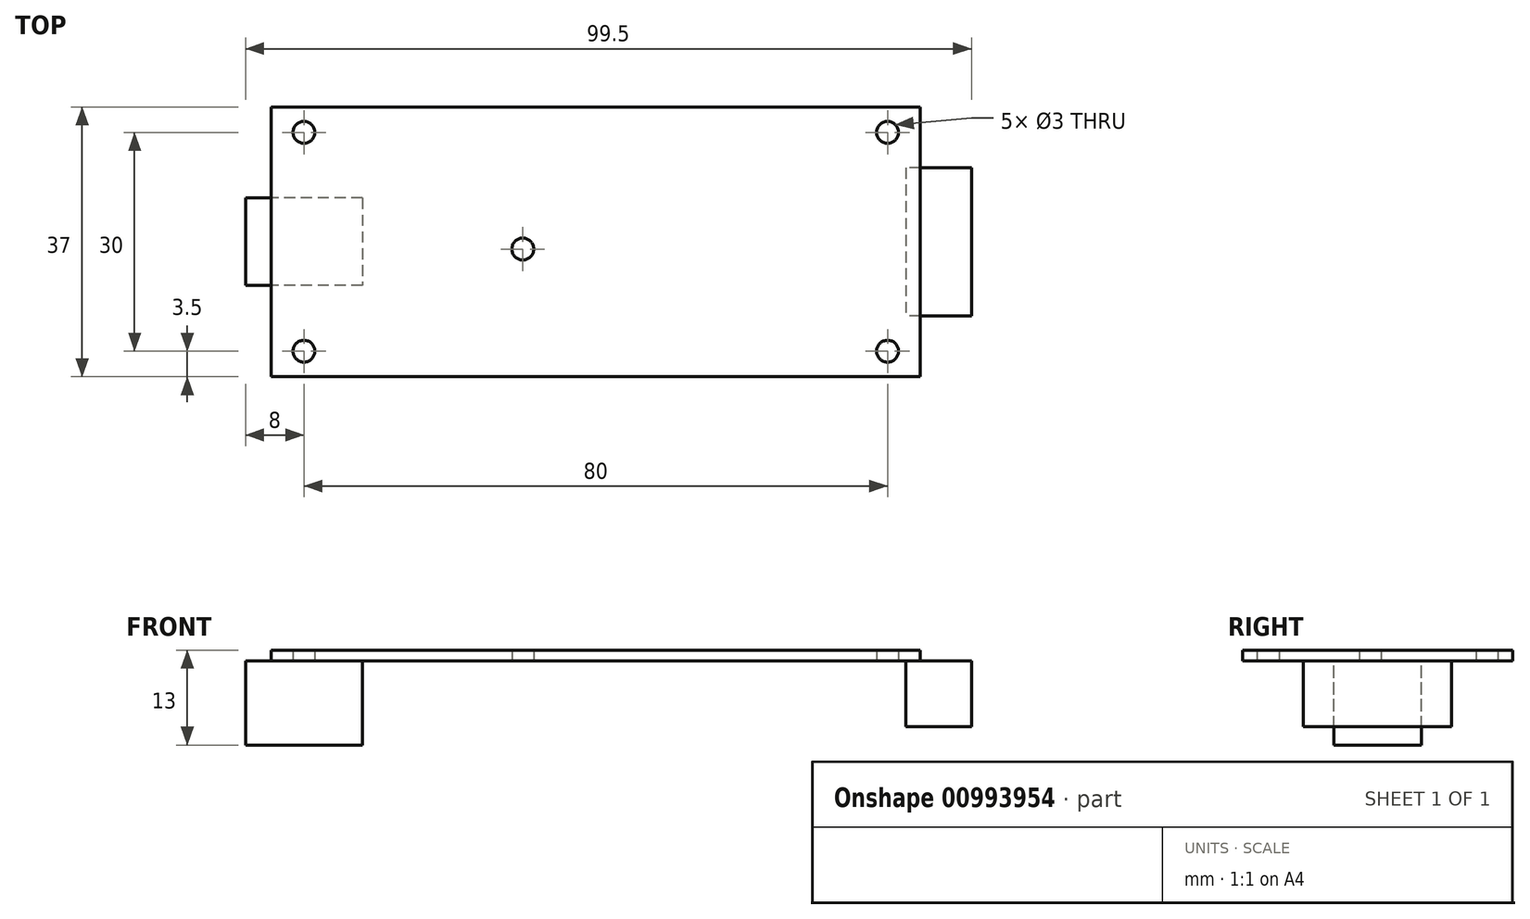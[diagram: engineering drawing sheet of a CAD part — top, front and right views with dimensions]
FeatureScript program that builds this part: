
annotation { "Feature Type Name" : "Feature", "Feature Type Description" : "" }
export const myFeature = defineFeature(function(context is Context, id is Id, definition is map)
    precondition{}
    {
        {
            var Q0;
            Q0=qCreatedBy(makeId("Top.planeOp"),FACE);
            var sketch = newSketch(context, id + "F0", { "sketchPlane" : qUnion([Q0])});
            skLineSegment(sketch, "E0.bottom", {"start": v(-44.5, 18.5) * mm, "end": v(44.5, 18.5) * mm});
            skLineSegment(sketch, "E0.top", {"start": v(-44.5, -18.5) * mm, "end": v(44.5, -18.5) * mm});
            skLineSegment(sketch, "E0.left", {"start": v(-44.5, 18.5) * mm, "end": v(-44.5, -18.5) * mm});
            skLineSegment(sketch, "E0.right", {"start": v(44.5, 18.5) * mm, "end": v(44.5, -18.5) * mm});
            skLineSegment(sketch, "E1", {"start": v(-44.5, 10.1) * mm, "end": v(0, 10.1) * mm, "construction": true});
            skLineSegment(sketch, "E2", {"start": v(0, 10.1) * mm, "end": v(44.5, 10.1) * mm, "construction": true});
            skLineSegment(sketch, "E3", {"start": v(-17.79, 18.5) * mm, "end": v(-17.79, 0) * mm, "construction": true});
            skLineSegment(sketch, "E4", {"start": v(-17.79, 0) * mm, "end": v(-17.79, -18.5) * mm, "construction": true});
            skCircle(sketch, "E5", {"center": v(-40, 15) * mm, "radius": 1.5 * mm});
            skCircle(sketch, "E6.MirrorC", {"center": v(40, 15) * mm, "radius": 1.5 * mm});
            skCircle(sketch, "E7.MirrorC", {"center": v(-40, -15) * mm, "radius": 1.5 * mm});
            skCircle(sketch, "E8.MirrorC", {"center": v(40, -15) * mm, "radius": 1.5 * mm});
            skCircle(sketch, "E9", {"center": v(-10, -1) * mm, "radius": 1.5 * mm});
            skLineSegment(sketch, "E10", {"start": v(-10, -18.5) * mm, "end": v(-10, 18.5) * mm, "construction": true});
            skLineSegment(sketch, "E11", {"start": v(44.5, -1) * mm, "end": v(-44.5, -1) * mm, "construction": true});
            skSolve(sketch);
        }
        {
            var Q0;
            Q0=makeQuery(id+"F0.imprint","IMPRINT",FACE,{"disambiguationData":[TD([[makeQuery(id+"F0.imprint","IMPRINT",EDGE,{"derivedFrom":sQuery(id+"F0.wireOp",EDGE,"E0.bottom")}),-1.0]])]});
            extrude(context, id + "F1", {"entities" : qUnion([Q0]), "depth" : 1.5 * mm, "offsetDistance" : 25 * mm});
        }
        {
            var Q0;
            Q0=makeQuery(id+"F1.opExtrude","CAP_FACE",FACE,{"disambiguationData":[OSD([sQuery(id+"F0.wireOp",EDGE,"E0.bottom"),sQuery(id+"F0.wireOp",EDGE,"E0.top"),sQuery(id+"F0.wireOp",EDGE,"E0.left"),sQuery(id+"F0.wireOp",EDGE,"E0.right"),sQuery(id+"F0.wireOp",EDGE,"E5"),sQuery(id+"F0.wireOp",EDGE,"E6.MirrorC"),sQuery(id+"F0.wireOp",EDGE,"E7.MirrorC"),sQuery(id+"F0.wireOp",EDGE,"E8.MirrorC"),sQuery(id+"F0.wireOp",EDGE,"E9")])],"isStart":true});
            var sketch = newSketch(context, id + "F2", { "sketchPlane" : qUnion([Q0])});
            skLineSegment(sketch, "E12.bottom", {"start": v(-32, -6) * mm, "end": v(-48, -6) * mm});
            skLineSegment(sketch, "E12.top", {"start": v(-32, 6) * mm, "end": v(-48, 6) * mm});
            skLineSegment(sketch, "E12.left", {"start": v(-32, -6) * mm, "end": v(-32, 6) * mm});
            skLineSegment(sketch, "E12.right", {"start": v(-48, -6) * mm, "end": v(-48, 6) * mm});
            skLineSegment(sketch, "E13", {"start": v(-36.96, -6) * mm, "end": v(-36.96, 0) * mm, "construction": true});
            skLineSegment(sketch, "E14", {"start": v(-36.96, 0) * mm, "end": v(-36.96, 6) * mm, "construction": true});
            skLineSegment(sketch, "E15.bottom", {"start": v(51.5, -10.15) * mm, "end": v(42.5, -10.15) * mm});
            skLineSegment(sketch, "E15.top", {"start": v(51.5, 10.15) * mm, "end": v(42.5, 10.15) * mm});
            skLineSegment(sketch, "E15.left", {"start": v(51.5, -10.15) * mm, "end": v(51.5, 10.15) * mm});
            skLineSegment(sketch, "E15.right", {"start": v(42.5, -10.15) * mm, "end": v(42.5, 10.15) * mm});
            skLineSegment(sketch, "E16", {"start": v(47, -10.15) * mm, "end": v(47, 0) * mm, "construction": true});
            skLineSegment(sketch, "E17", {"start": v(47, 0) * mm, "end": v(47, 10.15) * mm, "construction": true});
            skSolve(sketch);
        }
        {
            var Q0;
            {var subQ0=sQuery(id+"F2.wireOp",EDGE,"E12.left");Q0=makeQuery(id+"F2.imprint","IMPRINT",FACE,{"disambiguationData":[TD([[makeQuery(id+"F2.imprint","IMPRINT",EDGE,{"derivedFrom":subQ0}),1.0]])]});}
            var Q1;
            {var subQ0=sQuery(id+"F2.wireOp",EDGE,"E12.right");Q1=makeQuery(id+"F2.imprint","IMPRINT",FACE,{"disambiguationData":[TD([[makeQuery(id+"F2.imprint","IMPRINT",EDGE,{"derivedFrom":subQ0}),-1.0]])]});}
            extrude(context, id + "F3", {"entities" : qUnion([Q0, Q1]), "operationType" : NewBodyOperationType.ADD, "depth" : 11.5 * mm, "offsetDistance" : 25 * mm});
        }
        {
            var Q0;
            {var subQ0=sQuery(id+"F2.wireOp",EDGE,"E15.left");Q0=makeQuery(id+"F2.imprint","IMPRINT",FACE,{"disambiguationData":[TD([[makeQuery(id+"F2.imprint","IMPRINT",EDGE,{"derivedFrom":subQ0}),1.0]])]});}
            var Q1;
            {var subQ0=sQuery(id+"F2.wireOp",EDGE,"E15.right");Q1=makeQuery(id+"F2.imprint","IMPRINT",FACE,{"disambiguationData":[TD([[makeQuery(id+"F2.imprint","IMPRINT",EDGE,{"derivedFrom":subQ0}),-1.0]])]});}
            extrude(context, id + "F4", {"entities" : qUnion([Q0, Q1]), "operationType" : NewBodyOperationType.ADD, "depth" : 9 * mm, "offsetDistance" : 25 * mm});
        }
    });
